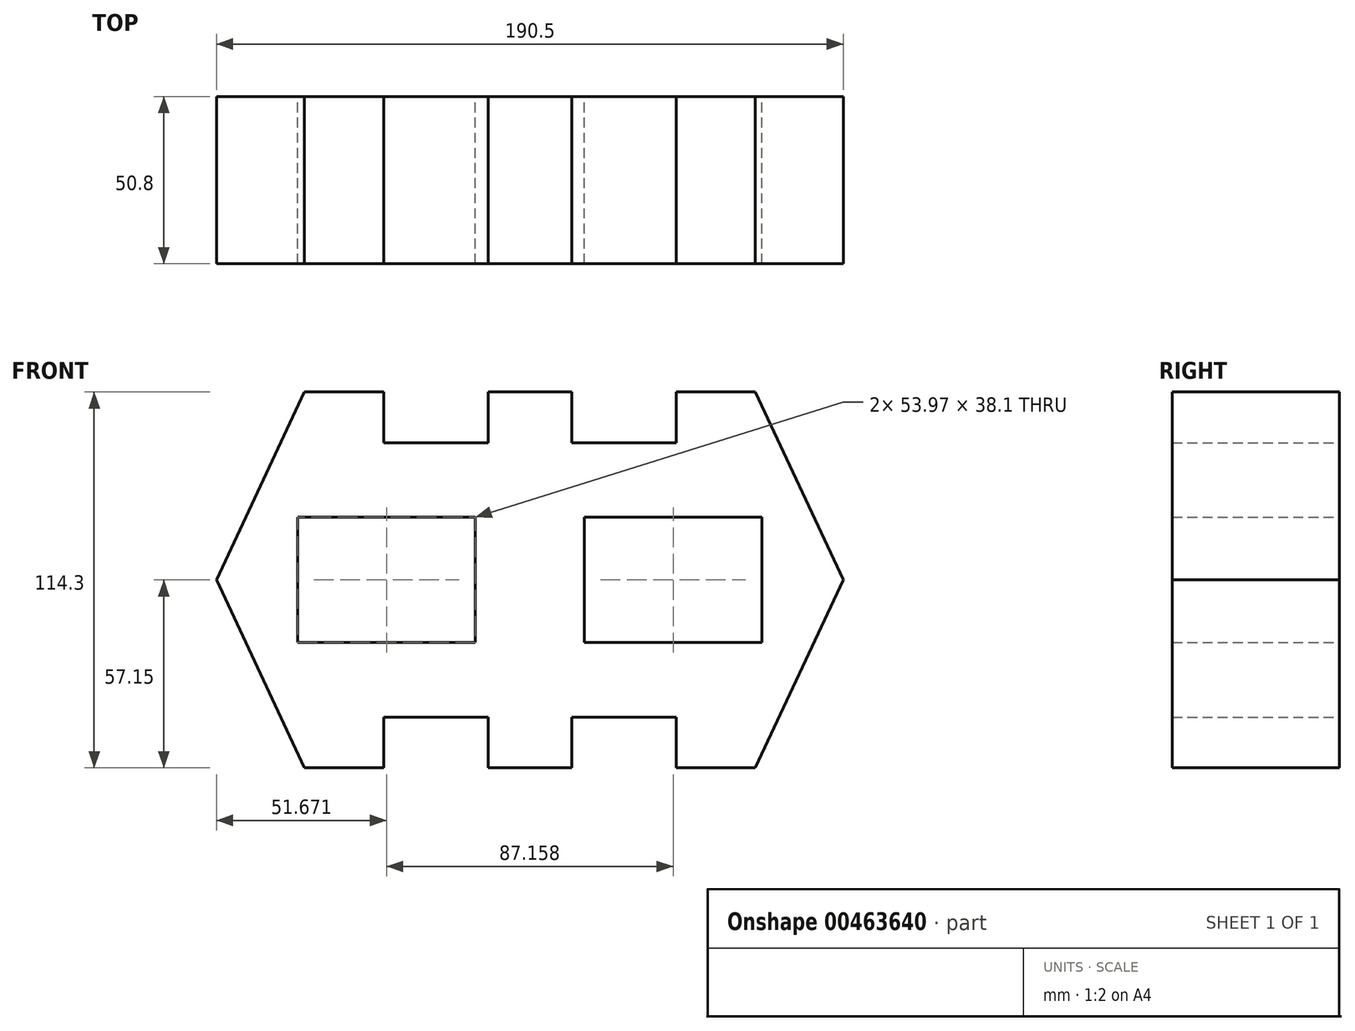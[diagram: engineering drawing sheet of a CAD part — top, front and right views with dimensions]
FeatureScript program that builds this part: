
annotation { "Feature Type Name" : "Feature", "Feature Type Description" : "" }
export const myFeature = defineFeature(function(context is Context, id is Id, definition is map)
    precondition{}
    {
        {
            var Q0;
            Q0=qCreatedBy(makeId("Front.planeOp"),FACE);
            var sketch = newSketch(context, id + "F0", { "sketchPlane" : qUnion([Q0])});
            skLineSegment(sketch, "E0", {"start": v(0, 0) * mm, "end": v(-12.7, 0) * mm});
            skLineSegment(sketch, "E1", {"start": v(-12.7, 0) * mm, "end": v(-12.7, -15.43) * mm});
            skLineSegment(sketch, "E2", {"start": v(-12.7, -15.43) * mm, "end": v(-44.45, -15.43) * mm});
            skLineSegment(sketch, "E3", {"start": v(-44.45, -15.43) * mm, "end": v(-44.45, 0) * mm});
            skLineSegment(sketch, "E4", {"start": v(-44.45, 0) * mm, "end": v(-68.52, 0) * mm});
            skLineSegment(sketch, "E5", {"start": v(-68.52, 0) * mm, "end": v(-95.25, -57.15) * mm});
            skLineSegment(sketch, "E6", {"start": v(-95.25, -57.15) * mm, "end": v(-68.53, -114.3) * mm});
            skLineSegment(sketch, "E7", {"start": v(-68.53, -114.3) * mm, "end": v(-44.45, -114.3) * mm});
            skLineSegment(sketch, "E8", {"start": v(-44.45, -114.3) * mm, "end": v(-44.45, -98.9) * mm});
            skLineSegment(sketch, "E9", {"start": v(-44.45, -98.9) * mm, "end": v(-12.7, -98.9) * mm});
            skLineSegment(sketch, "E10", {"start": v(-12.7, -98.9) * mm, "end": v(-12.7, -114.3) * mm});
            skLineSegment(sketch, "E11", {"start": v(-12.7, -114.3) * mm, "end": v(0, -114.3) * mm});
            skLineSegment(sketch, "E12.bottom", {"start": v(-70.57, -76.2) * mm, "end": v(-16.6, -76.2) * mm});
            skLineSegment(sketch, "E12.top", {"start": v(-70.57, -38.1) * mm, "end": v(-16.6, -38.1) * mm});
            skLineSegment(sketch, "E12.left", {"start": v(-70.57, -76.2) * mm, "end": v(-70.57, -38.1) * mm});
            skLineSegment(sketch, "E12.right", {"start": v(-16.6, -76.2) * mm, "end": v(-16.6, -38.1) * mm});
            skLineSegment(sketch, "E13", {"start": v(0, 0) * mm, "end": v(0, -114.3) * mm});
            skLineSegment(sketch, "E14.MirrorCS", {"start": v(0, 0) * mm, "end": v(12.7, 0) * mm});
            skLineSegment(sketch, "E15.MirrorCS", {"start": v(12.7, 0) * mm, "end": v(12.7, -15.43) * mm});
            skLineSegment(sketch, "E16.MirrorCS", {"start": v(12.7, -15.43) * mm, "end": v(44.45, -15.43) * mm});
            skLineSegment(sketch, "E17.MirrorCS", {"start": v(44.45, -15.43) * mm, "end": v(44.45, 0) * mm});
            skLineSegment(sketch, "E18.MirrorCS", {"start": v(44.45, 0) * mm, "end": v(68.52, 0) * mm});
            skLineSegment(sketch, "E19.MirrorCS", {"start": v(68.52, 0) * mm, "end": v(95.25, -57.15) * mm});
            skLineSegment(sketch, "E20.MirrorCS", {"start": v(68.53, -114.3) * mm, "end": v(44.45, -114.3) * mm});
            skLineSegment(sketch, "E21.MirrorCS", {"start": v(44.45, -114.3) * mm, "end": v(44.45, -98.9) * mm});
            skLineSegment(sketch, "E22.MirrorCS", {"start": v(44.45, -98.9) * mm, "end": v(12.7, -98.9) * mm});
            skLineSegment(sketch, "E23.MirrorCS", {"start": v(12.7, -98.9) * mm, "end": v(12.7, -114.3) * mm});
            skLineSegment(sketch, "E24.MirrorCS", {"start": v(12.7, -114.3) * mm, "end": v(0, -114.3) * mm});
            skLineSegment(sketch, "E25.MirrorCS", {"start": v(70.57, -76.2) * mm, "end": v(16.6, -76.2) * mm});
            skLineSegment(sketch, "E26.MirrorCS", {"start": v(70.57, -38.1) * mm, "end": v(16.6, -38.1) * mm});
            skLineSegment(sketch, "E27.MirrorCS", {"start": v(70.57, -76.2) * mm, "end": v(70.57, -38.1) * mm});
            skLineSegment(sketch, "E28.MirrorCS", {"start": v(16.6, -76.2) * mm, "end": v(16.6, -38.1) * mm});
            skLineSegment(sketch, "E29.MirrorCS", {"start": v(95.25, -57.15) * mm, "end": v(68.53, -114.3) * mm});
            skSolve(sketch);
        }
        {
            var Q0;
            Q0 = qSketchRegion(id + "F0", true);
            var Q1;
            Q1=makeQuery(id+"F0.imprint","IMPRINT",FACE,{"disambiguationData":[TD([[makeQuery(id+"F0.imprint","IMPRINT",EDGE,{"derivedFrom":sQuery(id+"F0.wireOp",EDGE,"E0")}),1.0]])]});
            extrude(context, id + "F1", {"entities" : qUnion([Q0, Q1]), "depth" : 50.8 * mm});
        }
    });
